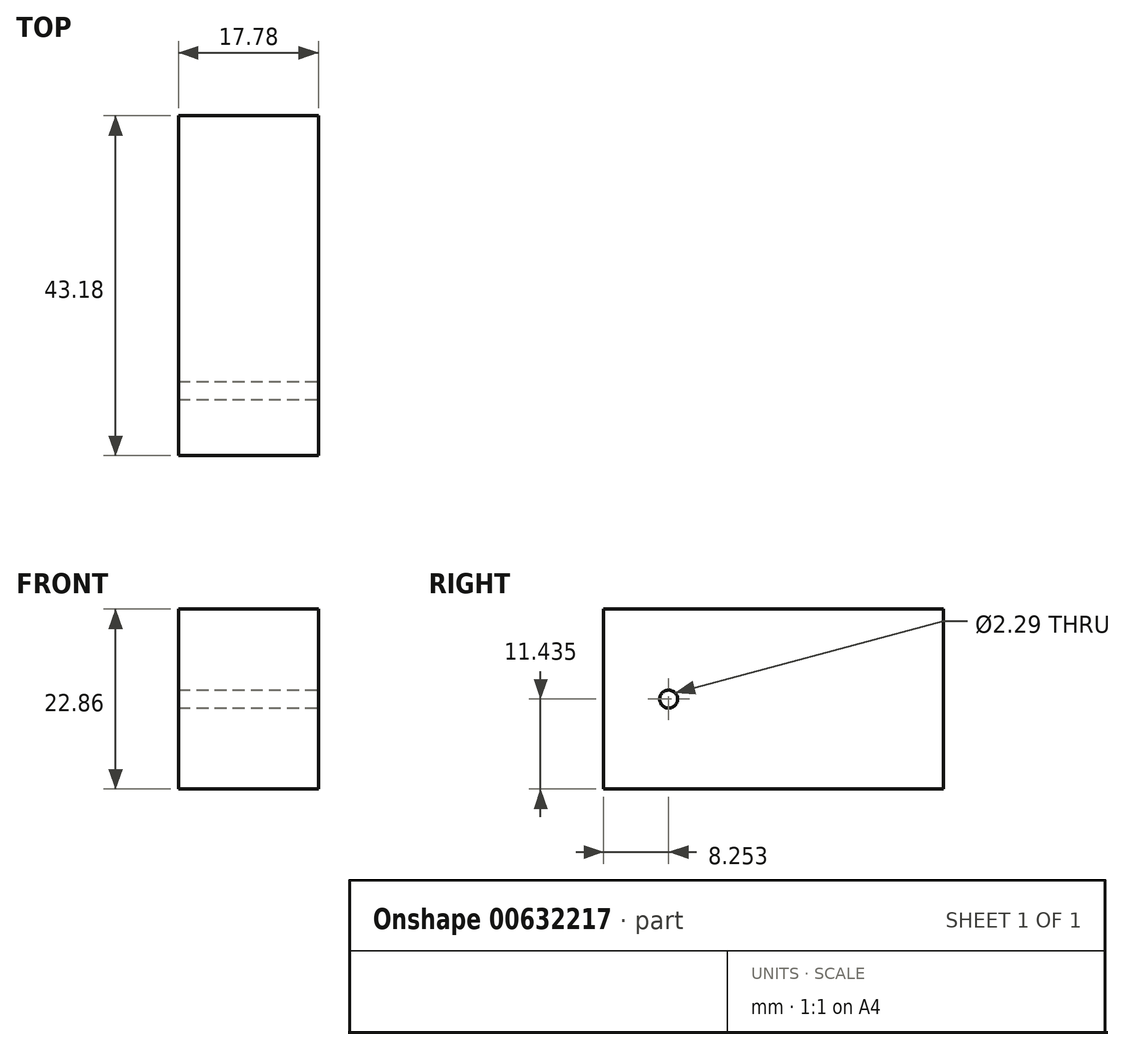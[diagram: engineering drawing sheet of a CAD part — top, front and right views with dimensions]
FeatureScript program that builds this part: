
annotation { "Feature Type Name" : "Feature", "Feature Type Description" : "" }
export const myFeature = defineFeature(function(context is Context, id is Id, definition is map)
    precondition{}
    {
        {
            var Q0;
            Q0=qCreatedBy(makeId("Front.planeOp"),FACE);
            var sketch = newSketch(context, id + "F0", { "sketchPlane" : qUnion([Q0])});
            skLineSegment(sketch, "E0.bottom", {"start": v(-6.1, 18.73) * mm, "end": v(11.69, 18.73) * mm});
            skLineSegment(sketch, "E0.top", {"start": v(-6.1, -4.13) * mm, "end": v(11.69, -4.13) * mm});
            skLineSegment(sketch, "E0.left", {"start": v(-6.1, 18.73) * mm, "end": v(-6.1, -4.13) * mm});
            skLineSegment(sketch, "E0.right", {"start": v(11.69, 18.73) * mm, "end": v(11.69, -4.13) * mm});
            skSolve(sketch);
        }
        {
            var Q0;
            Q0=makeQuery(id+"F0.imprint","IMPRINT",FACE,{"disambiguationData":[TD([[makeQuery(id+"F0.imprint","IMPRINT",EDGE,{"derivedFrom":sQuery(id+"F0.wireOp",EDGE,"E0.bottom")}),-1.0]])]});
            extrude(context, id + "F1", {"entities" : qUnion([Q0]), "depth" : 43.18 * mm, "offsetDistance" : 25.4 * mm});
        }
        {
            var Q0;
            Q0=makeQuery(id+"F1.opExtrude","SWEPT_FACE",FACE,{"disambiguationData":[OSD([sQuery(id+"F0.wireOp",EDGE,"E0.right")])]});
            var sketch = newSketch(context, id + "F2", { "sketchPlane" : qUnion([Q0])});
            skCircle(sketch, "E1", {"center": v(-34.93, 7.3) * mm, "radius": 1.14 * mm});
            skPoint(sketch, "E1.centerSnap0", {"position": v(-43.18, 7.3) * mm});
            skSolve(sketch);
        }
        {
            var Q0;
            Q0 = qSketchRegion(id + "F2", true);
            extrude(context, id + "F3", {"entities" : qUnion([Q0]), "operationType" : NewBodyOperationType.REMOVE, "oppositeDirection" : true, "depth" : 25.4 * mm, "offsetDistance" : 25.4 * mm});
        }
    });
